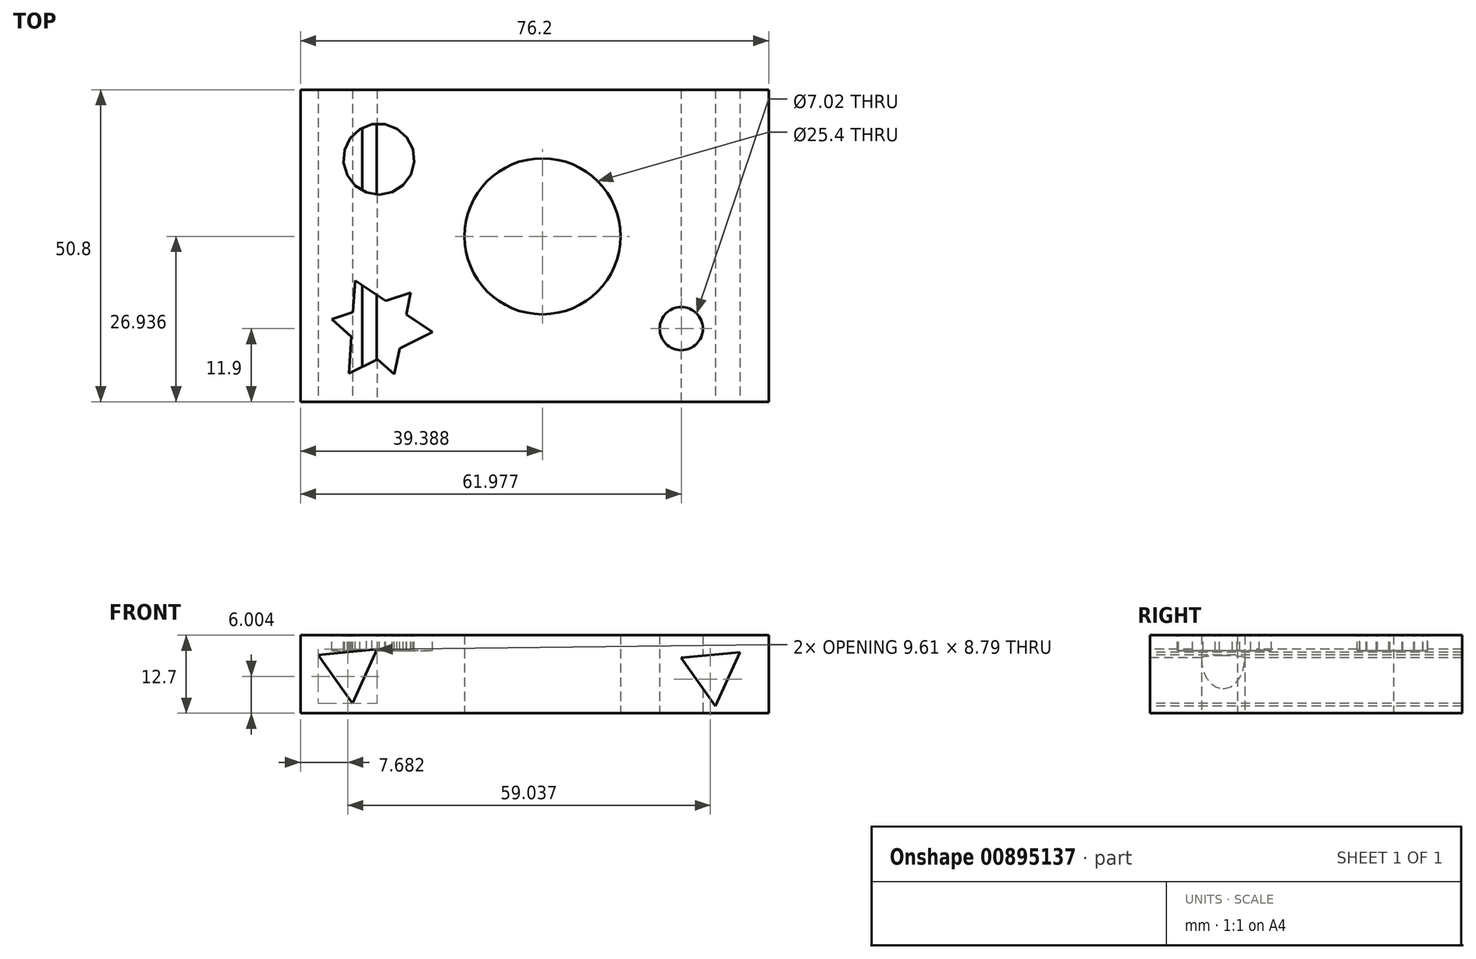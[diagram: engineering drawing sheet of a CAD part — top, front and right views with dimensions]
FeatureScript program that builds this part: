
annotation { "Feature Type Name" : "Feature", "Feature Type Description" : "" }
export const myFeature = defineFeature(function(context is Context, id is Id, definition is map)
    precondition{}
    {
        {
            var Q0;
            Q0=qCreatedBy(makeId("Top.planeOp"),FACE);
            var sketch = newSketch(context, id + "F0", { "sketchPlane" : qUnion([Q0])});
            skLineSegment(sketch, "E0.bottom", {"start": v(-17.99, -11.9) * mm, "end": v(-94.19, -11.9) * mm});
            skLineSegment(sketch, "E0.top", {"start": v(-17.99, 38.9) * mm, "end": v(-94.19, 38.9) * mm});
            skLineSegment(sketch, "E0.left", {"start": v(-17.99, -11.9) * mm, "end": v(-17.99, 38.9) * mm});
            skLineSegment(sketch, "E0.right", {"start": v(-94.19, -11.9) * mm, "end": v(-94.19, 38.9) * mm});
            skCircle(sketch, "E1", {"center": v(-54.8, 15.04) * mm, "radius": 12.7 * mm});
            skCircle(sketch, "E2", {"center": v(-32.21, 0) * mm, "radius": 3.51 * mm});
            skSolve(sketch);
        }
        {
            var Q0;
            Q0=makeQuery(id+"F0.imprint","IMPRINT",FACE,{"disambiguationData":[TD([[makeQuery(id+"F0.imprint","IMPRINT",EDGE,{"derivedFrom":sQuery(id+"F0.wireOp",EDGE,"E0.bottom")}),-1.0]])]});
            extrude(context, id + "F1", {"entities" : qUnion([Q0]), "depth" : 12.7 * mm, "offsetDistance" : 25.4 * mm});
        }
        {
            var Q0;
            Q0=makeQuery(id+"F1.opExtrude","CAP_FACE",FACE,{"disambiguationData":[OSD([sQuery(id+"F0.wireOp",EDGE,"E0.bottom"),sQuery(id+"F0.wireOp",EDGE,"E0.top"),sQuery(id+"F0.wireOp",EDGE,"E0.left"),sQuery(id+"F0.wireOp",EDGE,"E0.right"),sQuery(id+"F0.wireOp",EDGE,"E1"),sQuery(id+"F0.wireOp",EDGE,"E2")])],"isStart":false});
            var sketch = newSketch(context, id + "F2", { "sketchPlane" : qUnion([Q0])});
            skCircle(sketch, "E3.cCircle", {"center": v(-81.42, 27.6) * mm, "radius": 5.68 * mm, "construction": true});
            skLineSegment(sketch, "E3.0", {"start": v(-86.08, 31.02) * mm, "end": v(-84.53, 32.47) * mm});
            skLineSegment(sketch, "E3.1", {"start": v(-84.53, 32.47) * mm, "end": v(-82.56, 33.26) * mm});
            skLineSegment(sketch, "E3.2", {"start": v(-82.56, 33.26) * mm, "end": v(-80.44, 33.3) * mm});
            skLineSegment(sketch, "E3.3", {"start": v(-80.44, 33.3) * mm, "end": v(-78.45, 32.55) * mm});
            skLineSegment(sketch, "E3.4", {"start": v(-78.45, 32.55) * mm, "end": v(-76.86, 31.15) * mm});
            skLineSegment(sketch, "E3.5", {"start": v(-76.86, 31.15) * mm, "end": v(-75.89, 29.26) * mm});
            skLineSegment(sketch, "E3.6", {"start": v(-75.89, 29.26) * mm, "end": v(-75.66, 27.15) * mm});
            skLineSegment(sketch, "E3.7", {"start": v(-75.66, 27.15) * mm, "end": v(-76.22, 25.1) * mm});
            skLineSegment(sketch, "E3.8", {"start": v(-76.22, 25.1) * mm, "end": v(-77.47, 23.4) * mm});
            skLineSegment(sketch, "E3.9", {"start": v(-77.47, 23.4) * mm, "end": v(-79.26, 22.25) * mm});
            skLineSegment(sketch, "E3.10", {"start": v(-79.26, 22.25) * mm, "end": v(-81.34, 21.83) * mm});
            skLineSegment(sketch, "E3.11", {"start": v(-81.34, 21.83) * mm, "end": v(-83.43, 22.2) * mm});
            skLineSegment(sketch, "E3.12", {"start": v(-83.43, 22.2) * mm, "end": v(-85.25, 23.28) * mm});
            skLineSegment(sketch, "E3.13", {"start": v(-85.25, 23.28) * mm, "end": v(-86.55, 24.96) * mm});
            skLineSegment(sketch, "E3.14", {"start": v(-86.55, 24.96) * mm, "end": v(-87.16, 27) * mm});
            skLineSegment(sketch, "E3.15", {"start": v(-87.16, 27) * mm, "end": v(-87, 29.1) * mm});
            skLineSegment(sketch, "E3.16", {"start": v(-87, 29.1) * mm, "end": v(-86.08, 31.02) * mm});
            skPoint(sketch, "E3.0.midPoint", {"position": v(-85.3, 31.74) * mm});
            skCircle(sketch, "E4.cCircle", {"center": v(-81.42, 27.6) * mm, "radius": 9.13 * mm, "construction": true});
            skLineSegment(sketch, "E4.0", {"start": v(-91.86, 26.13) * mm, "end": v(-87.92, 35.9) * mm});
            skLineSegment(sketch, "E4.1", {"start": v(-87.92, 35.9) * mm, "end": v(-77.48, 37.39) * mm});
            skLineSegment(sketch, "E4.2", {"start": v(-77.48, 37.39) * mm, "end": v(-70.98, 29.08) * mm});
            skLineSegment(sketch, "E4.3", {"start": v(-70.98, 29.08) * mm, "end": v(-74.92, 19.3) * mm});
            skLineSegment(sketch, "E4.4", {"start": v(-74.92, 19.3) * mm, "end": v(-85.36, 17.82) * mm});
            skLineSegment(sketch, "E4.5", {"start": v(-85.36, 17.82) * mm, "end": v(-91.86, 26.13) * mm});
            skPoint(sketch, "E4.0.midPoint", {"position": v(-89.9, 31.02) * mm});
            skCircle(sketch, "E5.cCircle", {"center": v(-81.42, 27.6) * mm, "radius": 11.28 * mm, "construction": true});
            skLineSegment(sketch, "E5.0", {"start": v(-94.44, 27.63) * mm, "end": v(-87.9, 38.9) * mm});
            skLineSegment(sketch, "E5.1", {"start": v(-87.9, 38.9) * mm, "end": v(-74.88, 38.87) * mm});
            skLineSegment(sketch, "E5.2", {"start": v(-74.88, 38.87) * mm, "end": v(-68.4, 27.58) * mm});
            skLineSegment(sketch, "E5.3", {"start": v(-68.4, 27.58) * mm, "end": v(-74.93, 16.31) * mm});
            skLineSegment(sketch, "E5.4", {"start": v(-74.93, 16.31) * mm, "end": v(-87.96, 16.34) * mm});
            skLineSegment(sketch, "E5.5", {"start": v(-87.96, 16.34) * mm, "end": v(-94.44, 27.63) * mm});
            skPoint(sketch, "E5.0.midPoint", {"position": v(-91.17, 33.26) * mm});
            skCircle(sketch, "E6.cCircle", {"center": v(-81.41, 0) * mm, "radius": 12.52 * mm, "construction": true});
            skLineSegment(sketch, "E6.0", {"start": v(-85.28, -11.9) * mm, "end": v(-93.93, 0) * mm});
            skLineSegment(sketch, "E6.1", {"start": v(-93.93, 0) * mm, "end": v(-85.28, 11.9) * mm});
            skLineSegment(sketch, "E6.2", {"start": v(-85.28, 11.9) * mm, "end": v(-71.29, 7.36) * mm});
            skLineSegment(sketch, "E6.3", {"start": v(-71.29, 7.36) * mm, "end": v(-71.29, -7.36) * mm});
            skLineSegment(sketch, "E6.4", {"start": v(-71.29, -7.36) * mm, "end": v(-85.28, -11.9) * mm});
            skCircle(sketch, "E7.cCircle", {"center": v(-81.41, 0) * mm, "radius": 8.76 * mm, "construction": true});
            skLineSegment(sketch, "E7.0", {"start": v(-85.28, 7.86) * mm, "end": v(-72.67, -0.58) * mm});
            skLineSegment(sketch, "E7.1", {"start": v(-72.67, -0.58) * mm, "end": v(-86.29, -7.28) * mm});
            skLineSegment(sketch, "E7.2", {"start": v(-86.29, -7.28) * mm, "end": v(-85.28, 7.86) * mm});
            skCircle(sketch, "E8.cCircle", {"center": v(-81.41, 0) * mm, "radius": 7.84 * mm, "construction": true});
            skLineSegment(sketch, "E8.0", {"start": v(-76.24, 5.9) * mm, "end": v(-78.9, -7.43) * mm});
            skLineSegment(sketch, "E8.1", {"start": v(-78.9, -7.43) * mm, "end": v(-89.1, 1.53) * mm});
            skLineSegment(sketch, "E8.2", {"start": v(-89.1, 1.53) * mm, "end": v(-76.24, 5.9) * mm});
            skSolve(sketch);
        }
        {
            var Q0;
            {var subQ1=sQuery(id+"F2.wireOp",EDGE,"E7.0");var subQ8=sQuery(id+"F2.wireOp",EDGE,"E8.2");var subQ11=makeQuery(id+"F2.imprint","INTERSECT",VERTEX,{"derivedFrom":[subQ1,subQ8]});Q0=makeQuery(id+"F2.imprint","IMPRINT",FACE,{"disambiguationData":[TD([[makeQuery(id+"F2.imprint","IMPRINT",EDGE,{"disambiguationData":[TD([[subQ11,-1.0]])],"derivedFrom":subQ1}),-1.0]])]});}
            var Q1;
            {var subQ0=sQuery(id+"F2.wireOp",EDGE,"E7.2");var subQ1=sQuery(id+"F2.wireOp",EDGE,"E7.0");var subQ2=makeQuery(id+"F2.imprint","INTERSECT",VERTEX,{"derivedFrom":[subQ1,subQ0]});Q1=makeQuery(id+"F2.imprint","IMPRINT",FACE,{"disambiguationData":[TD([[makeQuery(id+"F2.imprint","IMPRINT",EDGE,{"disambiguationData":[TD([[subQ2,-1.0]])],"derivedFrom":subQ1}),-1.0]])]});}
            var Q2;
            {var subQ0=sQuery(id+"F2.wireOp",EDGE,"E8.2");var subQ1=sQuery(id+"F2.wireOp",EDGE,"E7.0");var subQ2=makeQuery(id+"F2.imprint","INTERSECT",VERTEX,{"derivedFrom":[subQ1,subQ0]});Q2=makeQuery(id+"F2.imprint","IMPRINT",FACE,{"disambiguationData":[TD([[makeQuery(id+"F2.imprint","IMPRINT",EDGE,{"disambiguationData":[TD([[subQ2,-1.0]])],"derivedFrom":subQ1}),1.0]])]});}
            var Q3;
            {var subQ0=sQuery(id+"F2.wireOp",EDGE,"E7.1");var subQ1=sQuery(id+"F2.wireOp",EDGE,"E7.0");var subQ2=makeQuery(id+"F2.imprint","INTERSECT",VERTEX,{"derivedFrom":[subQ1,subQ0]});Q3=makeQuery(id+"F2.imprint","IMPRINT",FACE,{"disambiguationData":[TD([[makeQuery(id+"F2.imprint","IMPRINT",EDGE,{"disambiguationData":[TD([[subQ2,1.0]])],"derivedFrom":subQ1}),-1.0]])]});}
            var Q4;
            {var subQ0=sQuery(id+"F2.wireOp",EDGE,"E8.0");var subQ1=sQuery(id+"F2.wireOp",EDGE,"E7.1");var subQ2=makeQuery(id+"F2.imprint","INTERSECT",VERTEX,{"derivedFrom":[subQ1,subQ0]});Q4=makeQuery(id+"F2.imprint","IMPRINT",FACE,{"disambiguationData":[TD([[makeQuery(id+"F2.imprint","IMPRINT",EDGE,{"disambiguationData":[TD([[subQ2,-1.0]])],"derivedFrom":subQ1}),1.0]])]});}
            var Q5;
            {var subQ0=sQuery(id+"F2.wireOp",EDGE,"E7.2");var subQ1=sQuery(id+"F2.wireOp",EDGE,"E7.1");var subQ2=makeQuery(id+"F2.imprint","INTERSECT",VERTEX,{"derivedFrom":[subQ1,subQ0]});Q5=makeQuery(id+"F2.imprint","IMPRINT",FACE,{"disambiguationData":[TD([[makeQuery(id+"F2.imprint","IMPRINT",EDGE,{"disambiguationData":[TD([[subQ2,1.0]])],"derivedFrom":subQ1}),-1.0]])]});}
            var Q6;
            {var subQ0=sQuery(id+"F2.wireOp",EDGE,"E8.1");var subQ1=sQuery(id+"F2.wireOp",EDGE,"E7.2");var subQ2=makeQuery(id+"F2.imprint","INTERSECT",VERTEX,{"derivedFrom":[subQ1,subQ0]});Q6=makeQuery(id+"F2.imprint","IMPRINT",FACE,{"disambiguationData":[TD([[makeQuery(id+"F2.imprint","IMPRINT",EDGE,{"disambiguationData":[TD([[subQ2,-1.0]])],"derivedFrom":subQ1}),1.0]])]});}
            var Q7;
            Q7=makeQuery(id+"F2.imprint","IMPRINT",FACE,{"disambiguationData":[TD([[makeQuery(id+"F2.imprint","IMPRINT",EDGE,{"derivedFrom":sQuery(id+"F2.wireOp",EDGE,"E3.0")}),-1.0]])]});
            extrude(context, id + "F3", {"entities" : qUnion([Q0, Q1, Q2, Q3, Q4, Q5, Q6, Q7]), "operationType" : NewBodyOperationType.REMOVE, "oppositeDirection" : true, "depth" : 2.54 * mm, "offsetDistance" : 25.4 * mm});
        }
        {
            var Q0;
            Q0=makeQuery(id+"F1.opExtrude","SWEPT_FACE",FACE,{"disambiguationData":[OSD([sQuery(id+"F0.wireOp",EDGE,"E0.bottom")])]});
            var sketch = newSketch(context, id + "F4", { "sketchPlane" : qUnion([Q0])});
            skCircle(sketch, "E9.cCircle", {"center": v(-86.24, 7.16) * mm, "radius": 5.57 * mm});
            skLineSegment(sketch, "E9.0", {"start": v(-91.31, 9.46) * mm, "end": v(-81.7, 10.4) * mm});
            skLineSegment(sketch, "E9.1", {"start": v(-81.7, 10.4) * mm, "end": v(-85.7, 1.61) * mm});
            skLineSegment(sketch, "E9.2", {"start": v(-85.7, 1.61) * mm, "end": v(-91.31, 9.46) * mm});
            skCircle(sketch, "E10.cCircle", {"center": v(-27.2, 6.7) * mm, "radius": 5.57 * mm});
            skLineSegment(sketch, "E10.0", {"start": v(-32.27, 9) * mm, "end": v(-22.67, 9.94) * mm});
            skLineSegment(sketch, "E10.1", {"start": v(-22.67, 9.94) * mm, "end": v(-26.66, 1.15) * mm});
            skLineSegment(sketch, "E10.2", {"start": v(-26.66, 1.15) * mm, "end": v(-32.27, 9) * mm});
            skSolve(sketch);
        }
        {
            var Q0;
            Q0=makeQuery(id+"F4.imprint","IMPRINT",FACE,{"disambiguationData":[TD([[makeQuery(id+"F4.imprint","IMPRINT",EDGE,{"derivedFrom":sQuery(id+"F4.wireOp",EDGE,"E10.0")}),-1.0]])]});
            var Q1;
            Q1=makeQuery(id+"F4.imprint","IMPRINT",FACE,{"disambiguationData":[TD([[makeQuery(id+"F4.imprint","IMPRINT",EDGE,{"derivedFrom":sQuery(id+"F4.wireOp",EDGE,"E9.0")}),-1.0]])]});
            extrude(context, id + "F5", {"entities" : qUnion([Q0, Q1]), "operationType" : NewBodyOperationType.REMOVE, "oppositeDirection" : true, "depth" : 50.8 * mm, "offsetDistance" : 25.4 * mm});
        }
    });
